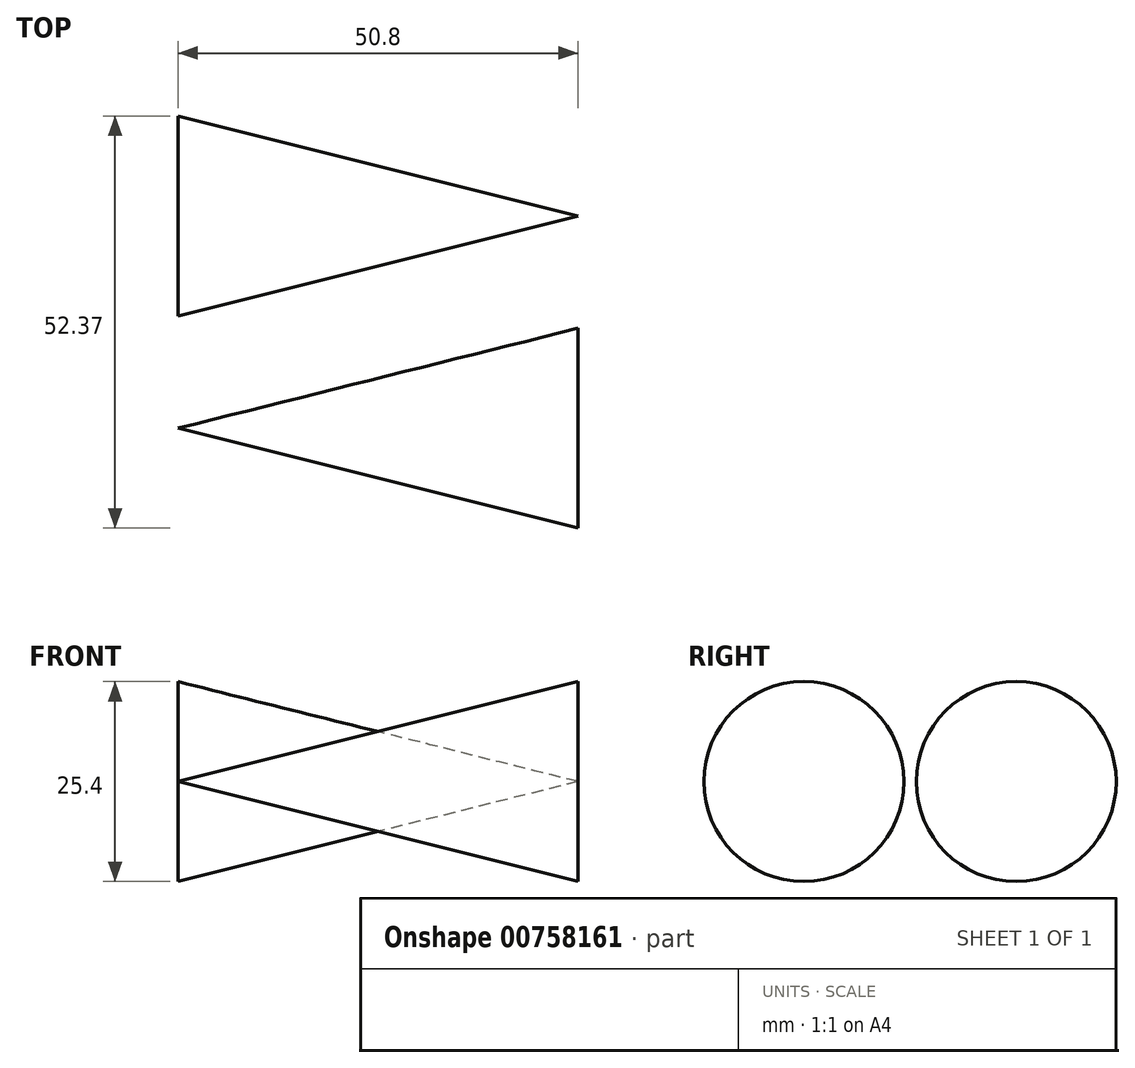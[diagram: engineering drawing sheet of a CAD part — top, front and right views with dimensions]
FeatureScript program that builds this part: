
annotation { "Feature Type Name" : "Feature", "Feature Type Description" : "" }
export const myFeature = defineFeature(function(context is Context, id is Id, definition is map)
    precondition{}
    {
        {
            var Q0;
            Q0=qCreatedBy(makeId("Top.planeOp"),FACE);
            var sketch = newSketch(context, id + "F0", { "sketchPlane" : qUnion([Q0])});
            skLineSegment(sketch, "E0", {"start": v(-50.8, 12.7) * mm, "end": v(-50.8, 0) * mm});
            skLineSegment(sketch, "E1", {"start": v(-50.8, 0) * mm, "end": v(0, 0) * mm});
            skLineSegment(sketch, "E2", {"start": v(0, 0) * mm, "end": v(-50.8, 12.7) * mm});
            skLineSegment(sketch, "E3", {"start": v(0, -14.27) * mm, "end": v(0, -26.97) * mm});
            skLineSegment(sketch, "E4", {"start": v(0, -26.97) * mm, "end": v(-50.8, -26.97) * mm});
            skLineSegment(sketch, "E5", {"start": v(-50.8, -26.97) * mm, "end": v(0, -14.27) * mm});
            skSolve(sketch);
        }
        {
            var Q0;
            Q0=makeQuery(id+"F0.imprint","IMPRINT",FACE,{"disambiguationData":[TD([[makeQuery(id+"F0.imprint","IMPRINT",EDGE,{"derivedFrom":sQuery(id+"F0.wireOp",EDGE,"E0")}),1.0]])]});
            var Q1;
            Q1=sQuery(id+"F0.wireOp",EDGE,"E1");
            revolve(context, id + "F1", {"surfaceOperationType" : NewSurfaceOperationType.NEW, "entities" : qUnion([Q0]), "axis" : qUnion([Q1]), "revolveType" : RevolveType.FULL});
        }
        {
            var Q0;
            Q0=makeQuery(id+"F0.imprint","IMPRINT",FACE,{"disambiguationData":[TD([[makeQuery(id+"F0.imprint","IMPRINT",EDGE,{"derivedFrom":sQuery(id+"F0.wireOp",EDGE,"E3")}),-1.0]])]});
            var Q1;
            Q1=sQuery(id+"F0.wireOp",EDGE,"E4");
            revolve(context, id + "F2", {"surfaceOperationType" : NewSurfaceOperationType.NEW, "entities" : qUnion([Q0]), "axis" : qUnion([Q1]), "revolveType" : RevolveType.FULL});
        }
    });
